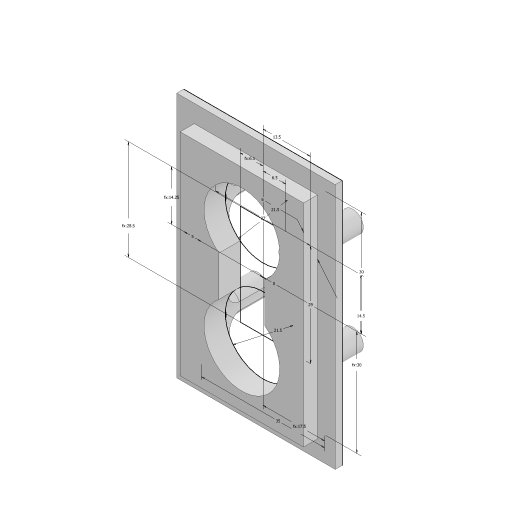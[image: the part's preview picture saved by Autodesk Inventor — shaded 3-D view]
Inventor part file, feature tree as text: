
AUTODESK INVENTOR PART (.ipt)
format: ipt  version: 2023 (Build 270158000, 158)  size: 235,520 bytes
history: native  units: mm
features: extrude x5, projected_geometry x4, sketch x2, fillet x1
ambient origin geometry x8: Origin, YZ Plane, XZ Plane, XY Plane, X Axis, Y Axis, Z Axis, Center Point
bodies: Solid1 (feature_tree)
feature tree (12):
  sketch  "Sketch1"  dims[d0=21.5mm d1=21.5mm]
  extrude  "Extrusion1"  Depth=21.5mm
  extrude  "Extrusion2"  Depth=4.0mm
  extrude  "Extrusion3"  TaperAngle=0.0deg  [1 undecoded]
  extrude  "Extrusion4"  Depth=4.0mm
  extrude  "Extrusion5"  Depth=4.0mm
  fillet  "Fillet1"  Radius=30.0mm
  sketch  "Sketch2"  dims[d2=28.5mm d3=14.25mm d6=0.0mm d13=35.0mm d14=17.5mm d15=30.0mm d16=30.0mm d17=5.0mm d18=2.0mm d19=0.0mm d20=6.0mm d21=0.0mm d22=6.5mm d23=6.5mm d24=6.0mm d25=14.5mm d26=13.5mm d27=0.0mm d28=0.0mm d29=12.0mm d30=0.0mm d31=4.1mm d32=5.0mm d33=-0.523599mm d34=20.0mm d36=27.0mm d37=20.0mm d39=29.0mm d42=4.1mm d43=4.1mm d44=4.1mm d45=4.0mm]
  projected_geometry  "Projected Loop1"
  projected_geometry  "Projected Loop2"
  projected_geometry  "Projected Loop3"
  projected_geometry  "Projected Loop4"
note: 1 required parameter value undecoded (feature->parameter linkage not recoverable at this tier; creation-order binding heuristic only, values carry confidence <= 0.55)
